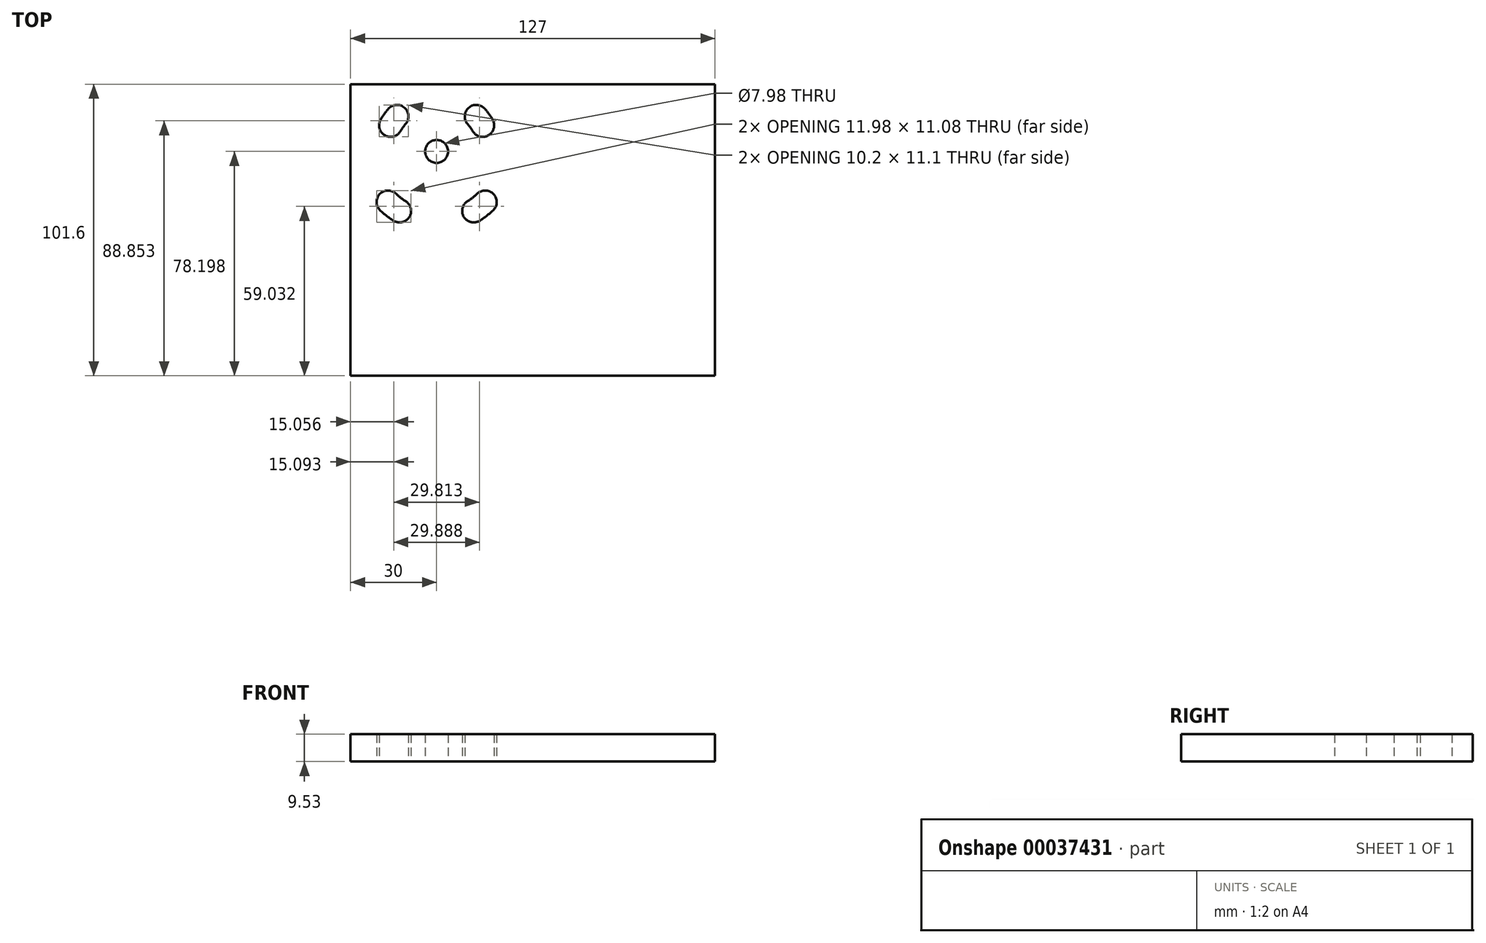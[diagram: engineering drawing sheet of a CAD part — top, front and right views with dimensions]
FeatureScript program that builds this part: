
annotation { "Feature Type Name" : "Feature", "Feature Type Description" : "" }
export const myFeature = defineFeature(function(context is Context, id is Id, definition is map)
    precondition{}
    {
        {
            var Q0;
            Q0=qCreatedBy(makeId("Top.planeOp"),FACE);
            var sketch = newSketch(context, id + "F0", { "sketchPlane" : qUnion([Q0])});
            skLineSegment(sketch, "E0.bottom", {"start": v(0, 0) * mm, "end": v(127, 0) * mm});
            skLineSegment(sketch, "E0.top", {"start": v(0, 101.6) * mm, "end": v(127, 101.6) * mm});
            skLineSegment(sketch, "E0.left", {"start": v(0, 0) * mm, "end": v(0, 101.6) * mm});
            skLineSegment(sketch, "E0.right", {"start": v(127, 0) * mm, "end": v(127, 101.6) * mm});
            skLineSegment(sketch, "E1", {"start": v(30, 101.6) * mm, "end": v(30, 0) * mm, "construction": true});
            skLineSegment(sketch, "E2", {"start": v(102, 101.6) * mm, "end": v(102, 0) * mm, "construction": true});
            skCircle(sketch, "E3", {"center": v(15, 88.9) * mm, "radius": 4 * mm, "construction": true});
            skCircle(sketch, "E4.0.1.0", {"center": v(15, 58.9) * mm, "radius": 4 * mm, "construction": true});
            skCircle(sketch, "E4.1.0.0", {"center": v(45, 88.9) * mm, "radius": 4 * mm, "construction": true});
            skCircle(sketch, "E4.1.1.0", {"center": v(45, 58.9) * mm, "radius": 4 * mm, "construction": true});
            skLineSegment(sketch, "E4.direction1", {"start": v(15, 88.9) * mm, "end": v(45, 88.9) * mm, "construction": true});
            skLineSegment(sketch, "E4.direction2", {"start": v(15, 88.9) * mm, "end": v(15, 58.9) * mm, "construction": true});
            skLineSegment(sketch, "E5", {"start": v(45, 88.9) * mm, "end": v(15, 58.9) * mm, "construction": true});
            skLineSegment(sketch, "E6", {"start": v(45, 58.9) * mm, "end": v(15, 88.9) * mm, "construction": true});
            skCircle(sketch, "E7", {"center": v(30, 73.9) * mm, "radius": 15.7 * mm, "construction": true});
            skCircle(sketch, "E8", {"center": v(41.1, 85) * mm, "radius": 1.9 * mm, "construction": true});
            skCircle(sketch, "E9", {"center": v(18.9, 85) * mm, "radius": 1.9 * mm, "construction": true});
            skCircle(sketch, "E10", {"center": v(30, 78.2) * mm, "radius": 11.11 * mm, "construction": true});
            skCircle(sketch, "E11", {"center": v(30, 78.2) * mm, "radius": 3.99 * mm});
            skCircle(sketch, "E12", {"center": v(30, 78.2) * mm, "radius": 24.44 * mm, "construction": true});
            skLineSegment(sketch, "E13", {"start": v(30, 78.2) * mm, "end": v(15, 58.9) * mm, "construction": true});
            skLineSegment(sketch, "E14", {"start": v(30, 78.2) * mm, "end": v(15, 88.9) * mm, "construction": true});
            skArc(sketch, "E15", {"start": v(13.06, 60.57) * mm, "mid": v(15, 58.9) * mm, "end": v(17.1, 57.44) * mm});
            skArc(sketch, "E16.0.startCap", {"start": v(10.3, 57.69) * mm, "mid": v(10.18, 63.35) * mm, "end": v(15.84, 63.46) * mm});
            skArc(sketch, "E16.0.endCap", {"start": v(19.21, 60.84) * mm, "mid": v(20.5, 55.33) * mm, "end": v(14.99, 54.04) * mm});
            skArc(sketch, "E16.0.left", {"start": v(15.84, 63.46) * mm, "mid": v(17.45, 62.06) * mm, "end": v(19.21, 60.84) * mm});
            skArc(sketch, "E16.0.right", {"start": v(10.3, 57.69) * mm, "mid": v(12.55, 55.74) * mm, "end": v(14.99, 54.04) * mm});
            skLineSegment(sketch, "E17", {"start": v(30, 78.2) * mm, "end": v(13.06, 60.57) * mm, "construction": true});
            skArc(sketch, "E18.MirrorCS", {"start": v(40.79, 60.84) * mm, "mid": v(39.5, 55.33) * mm, "end": v(45.01, 54.04) * mm});
            skArc(sketch, "E19.MirrorCS", {"start": v(49.7, 57.69) * mm, "mid": v(47.45, 55.74) * mm, "end": v(45.01, 54.04) * mm});
            skArc(sketch, "E20.MirrorCS", {"start": v(44.16, 63.46) * mm, "mid": v(42.55, 62.06) * mm, "end": v(40.79, 60.84) * mm});
            skArc(sketch, "E21.MirrorCS", {"start": v(49.7, 57.69) * mm, "mid": v(49.82, 63.35) * mm, "end": v(44.16, 63.46) * mm});
            skCircle(sketch, "E22", {"center": v(30, 78.2) * mm, "radius": 18.43 * mm, "construction": true});
            skArc(sketch, "E23", {"start": v(16.2, 90.4) * mm, "mid": v(15, 88.9) * mm, "end": v(13.96, 87.27) * mm});
            skArc(sketch, "E24.0.startCap", {"start": v(13.2, 93.06) * mm, "mid": v(18.85, 93.4) * mm, "end": v(19.2, 87.76) * mm});
            skArc(sketch, "E24.0.endCap", {"start": v(17.44, 85.3) * mm, "mid": v(12, 83.8) * mm, "end": v(10.48, 89.24) * mm});
            skArc(sketch, "E24.0.left", {"start": v(19.2, 87.76) * mm, "mid": v(18.26, 86.58) * mm, "end": v(17.44, 85.3) * mm});
            skArc(sketch, "E24.0.right", {"start": v(13.2, 93.06) * mm, "mid": v(11.74, 91.22) * mm, "end": v(10.48, 89.24) * mm});
            skArc(sketch, "E25.MirrorCS", {"start": v(46.8, 93.06) * mm, "mid": v(48.26, 91.22) * mm, "end": v(49.52, 89.24) * mm});
            skArc(sketch, "E26.MirrorCS", {"start": v(46.8, 93.06) * mm, "mid": v(41.15, 93.4) * mm, "end": v(40.8, 87.76) * mm});
            skArc(sketch, "E27.MirrorCS", {"start": v(40.8, 87.76) * mm, "mid": v(41.74, 86.58) * mm, "end": v(42.56, 85.3) * mm});
            skArc(sketch, "E28.MirrorCS", {"start": v(42.56, 85.3) * mm, "mid": v(48, 83.8) * mm, "end": v(49.52, 89.24) * mm});
            skLineSegment(sketch, "E29", {"start": v(30, 78.2) * mm, "end": v(16.2, 90.4) * mm, "construction": true});
            skLineSegment(sketch, "E30", {"start": v(16.2, 90.4) * mm, "end": v(13.06, 60.57) * mm, "construction": true});
            skSolve(sketch);
        }
        {
            var Q0;
            Q0=makeQuery(id+"F0.imprint","IMPRINT",FACE,{"disambiguationData":[TD([[makeQuery(id+"F0.imprint","IMPRINT",EDGE,{"derivedFrom":sQuery(id+"F0.wireOp",EDGE,"E0.bottom")}),1.0]])]});
            extrude(context, id + "F1", {"entities" : qUnion([Q0]), "depth" : 9.52 * mm});
        }
    });
